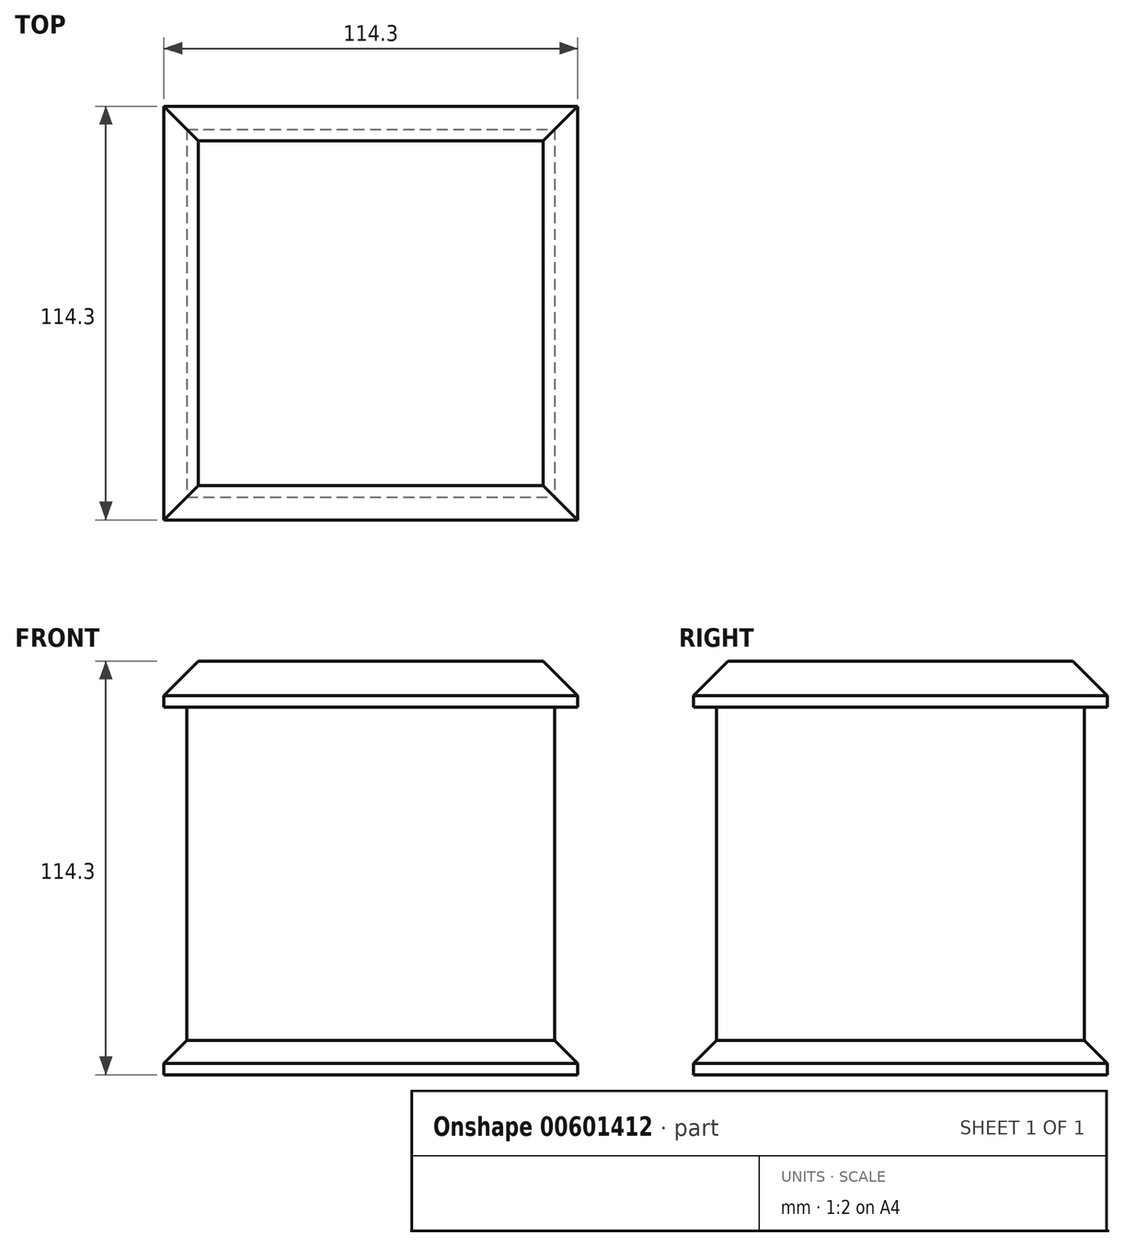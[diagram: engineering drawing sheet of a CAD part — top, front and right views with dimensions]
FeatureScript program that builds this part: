
annotation { "Feature Type Name" : "Feature", "Feature Type Description" : "" }
export const myFeature = defineFeature(function(context is Context, id is Id, definition is map)
    precondition{}
    {
        {
            var Q0;
            Q0=qCreatedBy(makeId("Front.planeOp"),FACE);
            var sketch = newSketch(context, id + "F0", { "sketchPlane" : qUnion([Q0])});
            skLineSegment(sketch, "E0.bottom", {"start": v(-50.8, 50.8) * mm, "end": v(50.8, 50.8) * mm});
            skLineSegment(sketch, "E0.top", {"start": v(-50.8, -50.8) * mm, "end": v(50.8, -50.8) * mm});
            skLineSegment(sketch, "E0.left", {"start": v(-50.8, 50.8) * mm, "end": v(-50.8, -50.8) * mm});
            skLineSegment(sketch, "E0.right", {"start": v(50.8, 50.8) * mm, "end": v(50.8, -50.8) * mm});
            skPoint(sketch, "E0.middle", {"position": v(0, 0) * mm});
            skLineSegment(sketch, "E1.bottom", {"start": v(-57.15, 57.15) * mm, "end": v(57.15, 57.15) * mm});
            skLineSegment(sketch, "E1.top", {"start": v(-57.15, 44.45) * mm, "end": v(57.15, 44.45) * mm});
            skLineSegment(sketch, "E1.left", {"start": v(-57.15, 57.15) * mm, "end": v(-57.15, 44.45) * mm});
            skLineSegment(sketch, "E1.right", {"start": v(57.15, 57.15) * mm, "end": v(57.15, 44.45) * mm});
            skPoint(sketch, "E1.middle", {"position": v(0, 50.8) * mm});
            skLineSegment(sketch, "E2.bottom", {"start": v(-57.15, -44.45) * mm, "end": v(57.15, -44.45) * mm});
            skLineSegment(sketch, "E2.top", {"start": v(-57.15, -57.15) * mm, "end": v(57.15, -57.15) * mm});
            skLineSegment(sketch, "E2.left", {"start": v(-57.15, -44.45) * mm, "end": v(-57.15, -57.15) * mm});
            skLineSegment(sketch, "E2.right", {"start": v(57.15, -44.45) * mm, "end": v(57.15, -57.15) * mm});
            skPoint(sketch, "E2.middle", {"position": v(0, -50.8) * mm});
            skSolve(sketch);
        }
        {
            var Q0;
            {var subQ0=sQuery(id+"F0.wireOp",EDGE,"E0.top");Q0=makeQuery(id+"F0.imprint","IMPRINT",FACE,{"disambiguationData":[TD([[makeQuery(id+"F0.imprint","IMPRINT",EDGE,{"derivedFrom":subQ0}),1.0]])]});}
            var Q1;
            {var subQ0=sQuery(id+"F0.wireOp",EDGE,"E1.top");var subQ1=sQuery(id+"F0.wireOp",EDGE,"E0.left");var subQ2=makeQuery(id+"F0.imprint","INTERSECT",VERTEX,{"derivedFrom":[subQ1,subQ0]});Q1=makeQuery(id+"F0.imprint","IMPRINT",FACE,{"disambiguationData":[TD([[makeQuery(id+"F0.imprint","IMPRINT",EDGE,{"disambiguationData":[TD([[subQ2,-1.0]])],"derivedFrom":subQ1}),1.0]])]});}
            var Q2;
            {var subQ0=sQuery(id+"F0.wireOp",EDGE,"E0.bottom");Q2=makeQuery(id+"F0.imprint","IMPRINT",FACE,{"disambiguationData":[TD([[makeQuery(id+"F0.imprint","IMPRINT",EDGE,{"derivedFrom":subQ0}),-1.0]])]});}
            extrude(context, id + "F1", {"entities" : qUnion([Q0, Q1, Q2]), "endBound" : BoundingType.SYMMETRIC, "depth" : 101.6 * mm, "offsetDistance" : 25.4 * mm});
        }
        {
            var Q0;
            {var subQ1=sQuery(id+"F0.wireOp",EDGE,"E0.bottom");Q0=makeQuery(id+"F0.imprint","IMPRINT",FACE,{"disambiguationData":[TD([[makeQuery(id+"F0.imprint","IMPRINT",EDGE,{"derivedFrom":subQ1}),1.0]])]});}
            var Q1;
            {var subQ1=sQuery(id+"F0.wireOp",EDGE,"E0.top");Q1=makeQuery(id+"F0.imprint","IMPRINT",FACE,{"disambiguationData":[TD([[makeQuery(id+"F0.imprint","IMPRINT",EDGE,{"derivedFrom":subQ1}),-1.0]])]});}
            extrude(context, id + "F2", {"entities" : qUnion([Q0, Q1]), "operationType" : NewBodyOperationType.ADD, "endBound" : BoundingType.SYMMETRIC, "oppositeDirection" : true, "depth" : 114.3 * mm, "offsetDistance" : 25.4 * mm});
        }
        {
            var Q0;
            {var subQ0=sQuery(id+"F0.wireOp",EDGE,"E0.bottom");Q0=makeQuery(id+"F0.imprint","IMPRINT",FACE,{"disambiguationData":[TD([[makeQuery(id+"F0.imprint","IMPRINT",EDGE,{"derivedFrom":subQ0}),-1.0]])]});}
            var Q1;
            {var subQ0=sQuery(id+"F0.wireOp",EDGE,"E0.top");Q1=makeQuery(id+"F0.imprint","IMPRINT",FACE,{"disambiguationData":[TD([[makeQuery(id+"F0.imprint","IMPRINT",EDGE,{"derivedFrom":subQ0}),1.0]])]});}
            extrude(context, id + "F3", {"entities" : qUnion([Q0, Q1]), "operationType" : NewBodyOperationType.ADD, "endBound" : BoundingType.SYMMETRIC, "depth" : 114.3 * mm, "offsetDistance" : 25.4 * mm});
        }
        {
            var Q0;
            Q0=makeQuery(id+"F2.opExtrude","CAP_EDGE",EDGE,{"disambiguationData":[OSD([sQuery(id+"F0.wireOp",EDGE,"E1.bottom")])],"isStart":true});
            var Q1;
            Q1=makeQuery(id+"F2.opExtrude","SWEPT_EDGE",EDGE,{"disambiguationData":[OSD([sQuery(id+"F0.wireOp",EDGE,"E1.bottom"),sQuery(id+"F0.wireOp",EDGE,"E1.right")])]});
            var Q2;
            Q2=makeQuery(id+"F2.opExtrude","CAP_EDGE",EDGE,{"disambiguationData":[OSD([sQuery(id+"F0.wireOp",EDGE,"E1.bottom")])],"isStart":false});
            var Q3;
            Q3=makeQuery(id+"F2.opExtrude","SWEPT_EDGE",EDGE,{"disambiguationData":[OSD([sQuery(id+"F0.wireOp",EDGE,"E1.bottom"),sQuery(id+"F0.wireOp",EDGE,"E1.left")])]});
            var Q4;
            Q4=makeQuery(id+"F2.opExtrude","SWEPT_EDGE",EDGE,{"disambiguationData":[OSD([sQuery(id+"F0.wireOp",EDGE,"E2.bottom"),sQuery(id+"F0.wireOp",EDGE,"E2.right")])]});
            var Q5;
            {var subQ0=sQuery(id+"F0.wireOp",EDGE,"E2.bottom");Q5=makeQuery(id+"F3.boolean.opBoolean","MERGE",EDGE,{"derivedFrom":[makeQuery(id+"F2.opExtrude","CAP_EDGE",EDGE,{"disambiguationData":[OSD([subQ0]),TDD([makeQuery(id+"F0.imprint","IMPRINT",EDGE,{"disambiguationData":[TD([[makeQuery(id+"F0.imprint","INTERSECT",VERTEX,{"derivedFrom":[subQ0,sQuery(id+"F0.wireOp",EDGE,"E2.left")]}),-1.0]])],"derivedFrom":subQ0})])],"isStart":true}),makeQuery(id+"F2.opExtrude","CAP_EDGE",EDGE,{"disambiguationData":[OSD([subQ0]),TDD([makeQuery(id+"F0.imprint","IMPRINT",EDGE,{"disambiguationData":[TD([[makeQuery(id+"F0.imprint","INTERSECT",VERTEX,{"derivedFrom":[subQ0,sQuery(id+"F0.wireOp",EDGE,"E2.right")]}),1.0]])],"derivedFrom":subQ0})])],"isStart":true}),makeQuery(id+"F3.opExtrude","CAP_EDGE",EDGE,{"disambiguationData":[OSD([subQ0])],"isStart":false})]});}
            var Q6;
            Q6=makeQuery(id+"F2.opExtrude","SWEPT_EDGE",EDGE,{"disambiguationData":[OSD([sQuery(id+"F0.wireOp",EDGE,"E2.bottom"),sQuery(id+"F0.wireOp",EDGE,"E2.left")])]});
            var Q7;
            {var subQ0=sQuery(id+"F0.wireOp",EDGE,"E2.bottom");Q7=makeQuery(id+"F3.boolean.opBoolean","MERGE",EDGE,{"derivedFrom":[makeQuery(id+"F2.opExtrude","CAP_EDGE",EDGE,{"disambiguationData":[OSD([subQ0]),TDD([makeQuery(id+"F0.imprint","IMPRINT",EDGE,{"disambiguationData":[TD([[makeQuery(id+"F0.imprint","INTERSECT",VERTEX,{"derivedFrom":[subQ0,sQuery(id+"F0.wireOp",EDGE,"E2.left")]}),-1.0]])],"derivedFrom":subQ0})])],"isStart":false}),makeQuery(id+"F2.opExtrude","CAP_EDGE",EDGE,{"disambiguationData":[OSD([subQ0]),TDD([makeQuery(id+"F0.imprint","IMPRINT",EDGE,{"disambiguationData":[TD([[makeQuery(id+"F0.imprint","INTERSECT",VERTEX,{"derivedFrom":[subQ0,sQuery(id+"F0.wireOp",EDGE,"E2.right")]}),1.0]])],"derivedFrom":subQ0})])],"isStart":false}),makeQuery(id+"F3.opExtrude","CAP_EDGE",EDGE,{"disambiguationData":[OSD([subQ0])],"isStart":true})]});}
            chamfer(context, id + "F4", {"entities" : qUnion([Q0, Q1, Q2, Q3, Q4, Q5, Q6, Q7]), "width" : 9.52 * mm, "tangentPropagation" : true});
        }
    });
